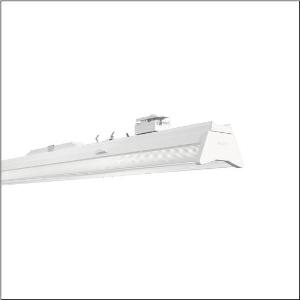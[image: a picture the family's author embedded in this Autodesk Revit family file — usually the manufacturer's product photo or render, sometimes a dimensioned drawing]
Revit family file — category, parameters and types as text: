
# Revit family: licross_21_performance_mo_51td16vn48xg
name_source: partatom
category: Lighting Fixtures
units: mm (PartAtom-declared; Revit-internal decimal feet)

## family parameters
Cut with Voids When Loaded = No
Host = Face
Light Source = No
Part Type = Normal
Room Calculation Point = No
Round Connector Dimension = Use Diameter
Shared = No

## types (1)
- --- (1 x LED, 8000 lm, 44.1 W, 4000K)
    Apparent Load = 44 VA
    CIE Flux Codes = 66 88 96 79 100
    Color Rendering = 80
    Color Temperature = 4000K
    Default Elevation = 1800 mm
    Description = Licross 21 Performance MO, luminaire insert, of sheet steel, galvanised, coil coated, white, length: 1.500mm, width: 120mm, height: 123mm, LED rated luminous flux: 8.000lm, light colour: 840, SDCM (Standard Deviation of Colour Matching)MacAdam ≤ 2 SDCM (initial), control gear: DALI 2, CLO, with plug, 5-pole, with phase selection, mains connection: 220..240V, AC, 50/60Hz, start of lifetime: 44W, end of service life: 49W, internal wiring halogen-free, primary light control with lens, of plastic, primary optical cover: cover, of PMMA, light emission: direct/indirect distribution, primary light characteristic: symmetric, protection rating (complete): IP54, insulation class (complete): insulation class I (protective earthing), certification: CE, ENEC, VDE, UKCA, protection symbol: D if used in an environment with non-conductive dust loads with corresponding accessories, impact resistance: IK06, permissible ambient temperature for indoor applications: -25..+35°C, corresponds to IFS (International Featured Standards) requirements for safety and quality in the food industry, reducing of maximum allowable ambient temperature of 5°C with ceiling mounting, LABS conformity tested according to VDMA 24364:2018-05, The light source and the operating device comply with the requirements of the Ecodesign Regulation (EU) 2019/2020 and are replaceable in accordance with this regulation, packaging unit: 1 piece
    Height = 114 mm
    Lamp = 1 x LED
    Lamp Light Flux = 8000 lm
    Lamp Power = 44.1 W
    Lamp count = 1
    Length = 1500 mm
    Luminous efficacy = 181 lm/W
    Manufacturer = Siteco
    ModVariant = No
    Model = 51TD16VN48XG
    Mounting Place = Ceiling
    Mounting Type = Pendant
    Number of Poles = 1
    OnlyDefault = Yes
    Power Factor = 1
    Product Name = Licross 21 Performance MO
    Product group = luminaire insert | ceiling pendant
    ProductGroupID = 901
    Protection Class = Protection class I
    Protection Degree = IP 54
    RLX_Detail_Level = 1
    RLX_Emergency_Light_Flux = 0 lm
    RLX_Emergency_Type = 0
    RLX_Emergency_Type_DB = No
    RlxData = <blob elided: 34309 chars, md5=f9a27349>
    Socket = socket
    Standby Power = 0 W
    System Light Flux = 8000 lm
    System Power = 44 W
    Type Comments = factory setting: luminous flux: 100 % | dim-lin: 254 | 294 mA
    Type Image = l_1256138.jpg
    URL = http://relux.com
    VarID = @adj_001211
    Voltage = 0 V
    Weight = 0.00 kg
    Width = 120 mm

## geometry (parser evidence)
native form markers: Blend x4, Sweep x12
no freeform markers — native parametric forms only
